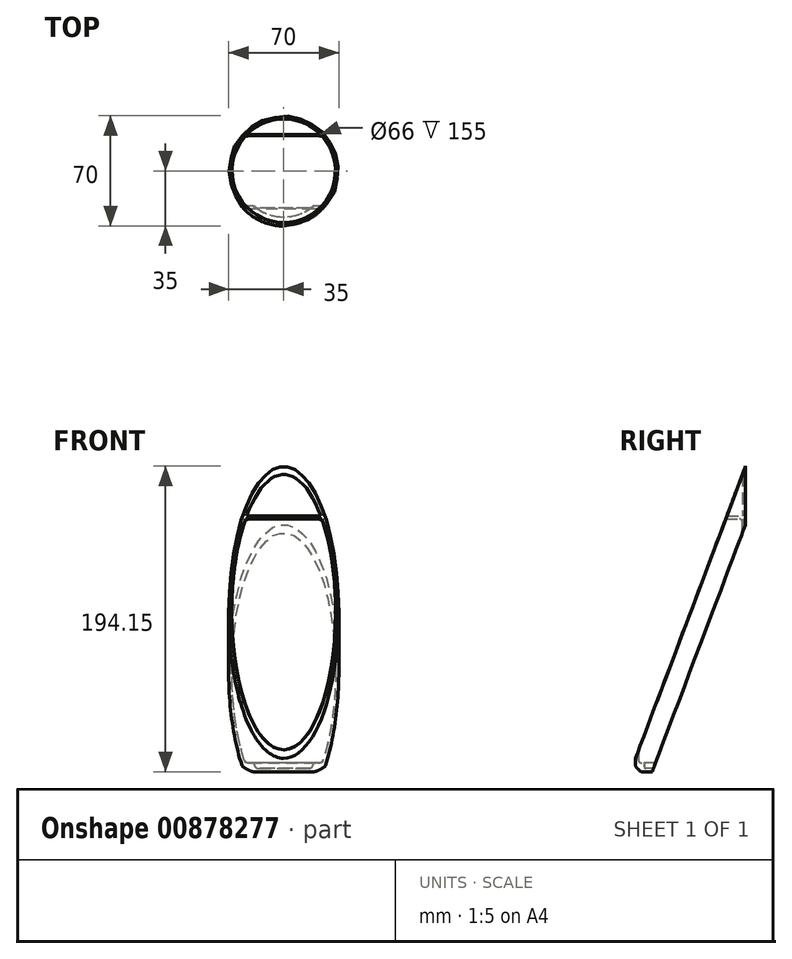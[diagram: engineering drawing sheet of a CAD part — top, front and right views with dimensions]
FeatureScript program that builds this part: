
annotation { "Feature Type Name" : "Feature", "Feature Type Description" : "" }
export const myFeature = defineFeature(function(context is Context, id is Id, definition is map)
    precondition{}
    {
        {
            var Q0;
            Q0=qCreatedBy(makeId("Front.planeOp"),FACE);
            var sketch = newSketch(context, id + "F0", { "sketchPlane" : qUnion([Q0])});
            skLineSegment(sketch, "E0", {"start": v(0, 0) * mm, "end": v(29.25, 0) * mm});
            skLineSegment(sketch, "E1", {"start": v(29.25, 0) * mm, "end": v(29.25, 3.5) * mm});
            skLineSegment(sketch, "E2", {"start": v(29.25, 3.5) * mm, "end": v(33, 3.5) * mm});
            skLineSegment(sketch, "E3", {"start": v(33, 3.5) * mm, "end": v(33, 158.5) * mm});
            skLineSegment(sketch, "E4", {"start": v(33, 158.5) * mm, "end": v(0, 158.5) * mm});
            skLineSegment(sketch, "E5", {"start": v(0, 158.5) * mm, "end": v(0, 0) * mm});
            skSolve(sketch);
        }
        {
            var Q0;
            Q0 = qSketchRegion(id + "F0", true);
            var Q1;
            Q1=sQuery(id+"F0.wireOp",EDGE,"E5");
            revolve(context, id + "F1", {"surfaceOperationType" : NewSurfaceOperationType.NEW, "entities" : qUnion([Q0]), "axis" : qUnion([Q1]), "revolveType" : RevolveType.FULL});
        }
        {
            var Q0;
            Q0=qCreatedBy(makeId("Front.planeOp"),FACE);
            var sketch = newSketch(context, id + "F2", { "sketchPlane" : qUnion([Q0])});
            skLineSegment(sketch, "E6", {"start": v(0, 160.5) * mm, "end": v(33, 160.5) * mm});
            skLineSegment(sketch, "E7", {"start": v(35, 193.5) * mm, "end": v(35, -2) * mm});
            skLineSegment(sketch, "E8", {"start": v(35, -2) * mm, "end": v(0, -2) * mm});
            skLineSegment(sketch, "E9", {"start": v(0, 193.5) * mm, "end": v(35, 193.5) * mm});
            skLineSegment(sketch, "E10", {"start": v(0, 190.5) * mm, "end": v(33, 190.5) * mm});
            skLineSegment(sketch, "E11", {"start": v(33, 190.5) * mm, "end": v(33, 160.5) * mm});
            skLineSegment(sketch, "E12", {"start": v(0, 190.5) * mm, "end": v(0, 193.5) * mm});
            skLineSegment(sketch, "E13", {"start": v(0, 160.5) * mm, "end": v(0, 158.5) * mm});
            skLineSegment(sketch, "E14", {"start": v(0, 158.5) * mm, "end": v(33, 158.5) * mm});
            skLineSegment(sketch, "E15", {"start": v(33, 158.5) * mm, "end": v(33, 3.5) * mm});
            skLineSegment(sketch, "E16", {"start": v(33, 3.5) * mm, "end": v(29.25, 3.5) * mm});
            skLineSegment(sketch, "E17", {"start": v(29.25, 3.5) * mm, "end": v(29.25, 0) * mm});
            skLineSegment(sketch, "E18", {"start": v(29.25, 0) * mm, "end": v(0, 0) * mm});
            skLineSegment(sketch, "E19", {"start": v(0, 0) * mm, "end": v(0, -2) * mm});
            skSolve(sketch);
        }
        {
            var Q0;
            Q0=makeQuery(id+"F1.opRevolve","SWEPT_EDGE",EDGE,{"disambiguationData":[OSD([sQuery(id+"F0.wireOp",EDGE,"E3"),sQuery(id+"F0.wireOp",EDGE,"E4")])]});
            var Q1;
            Q1=makeQuery(id+"F1.opRevolve","SWEPT_EDGE",EDGE,{"disambiguationData":[OSD([sQuery(id+"F0.wireOp",EDGE,"E2"),sQuery(id+"F0.wireOp",EDGE,"E3")])]});
            fillet(context, id + "F3", {"entities" : qUnion([Q0, Q1]), "radius" : 2 * mm, "tangentPropagation" : true, "allowEdgeOverflow" : false});
        }
        {
            var Q0;
            Q0=makeQuery(id+"F1.opRevolve","SWEPT_EDGE",EDGE,{"disambiguationData":[OSD([sQuery(id+"F0.wireOp",EDGE,"E0"),sQuery(id+"F0.wireOp",EDGE,"E1")])]});
            fillet(context, id + "F4", {"entities" : qUnion([Q0]), "radius" : 1 * mm, "tangentPropagation" : true, "allowEdgeOverflow" : false});
        }
        {
            var Q0;
            Q0 = qSketchRegion(id + "F2", true);
            var Q1;
            Q1=sQuery(id+"F2.wireOp",EDGE,"E12");
            revolve(context, id + "F5", {"surfaceOperationType" : NewSurfaceOperationType.NEW, "entities" : qUnion([Q0]), "axis" : qUnion([Q1]), "revolveType" : RevolveType.FULL});
        }
        {
            var Q0;
            Q0=qCreatedBy(makeId("Right.planeOp"),FACE);
            var sketch = newSketch(context, id + "F6", { "sketchPlane" : qUnion([Q0])});
            skLineSegment(sketch, "E20", {"start": v(35, 155.3) * mm, "end": v(-24.31, -2) * mm});
            skLineSegment(sketch, "E21", {"start": v(55.42, 246.3) * mm, "end": v(-38.2, -2) * mm});
            skPoint(sketch, "E22", {"position": v(-35, -2) * mm});
            skLineSegment(sketch, "E23", {"start": v(0, 0) * mm, "end": v(0, 48.82) * mm, "construction": true});
            skLineSegment(sketch, "E24", {"start": v(35, 155.3) * mm, "end": v(35, -2) * mm});
            skLineSegment(sketch, "E25", {"start": v(35, -2) * mm, "end": v(-24.31, -2) * mm});
            skLineSegment(sketch, "E26", {"start": v(55.42, 246.3) * mm, "end": v(-38.2, 246.3) * mm});
            skLineSegment(sketch, "E27", {"start": v(-38.2, 246.3) * mm, "end": v(-38.2, -2) * mm});
            skPoint(sketch, "E28", {"position": v(33, 158.5) * mm});
            skSolve(sketch);
        }
        {
            var Q0;
            Q0 = qSketchRegion(id + "F6", true);
            extrude(context, id + "F7", {"entities" : qUnion([Q0]), "operationType" : NewBodyOperationType.REMOVE, "endBound" : BoundingType.THROUGH_ALL, "depth" : 25 * mm, "offsetDistance" : 25 * mm, "hasSecondDirection" : true, "secondDirectionBound" : SecondDirectionBoundingType.THROUGH_ALL, "secondDirectionOppositeDirection" : true, "secondDirectionDepth" : 25 * mm});
        }
        {
            var Q0;
            Q0=makeQuery(id+"F5.opRevolve","SWEPT_EDGE",EDGE,{"disambiguationData":[OSD([sQuery(id+"F2.wireOp",EDGE,"E7"),sQuery(id+"F2.wireOp",EDGE,"E8")])]});
            fillet(context, id + "F8", {"entities" : qUnion([Q0]), "radius" : 4 * mm, "tangentPropagation" : true, "rho" : .2, "crossSection" : FilletCrossSection.CONIC, "allowEdgeOverflow" : false});
        }
    });
